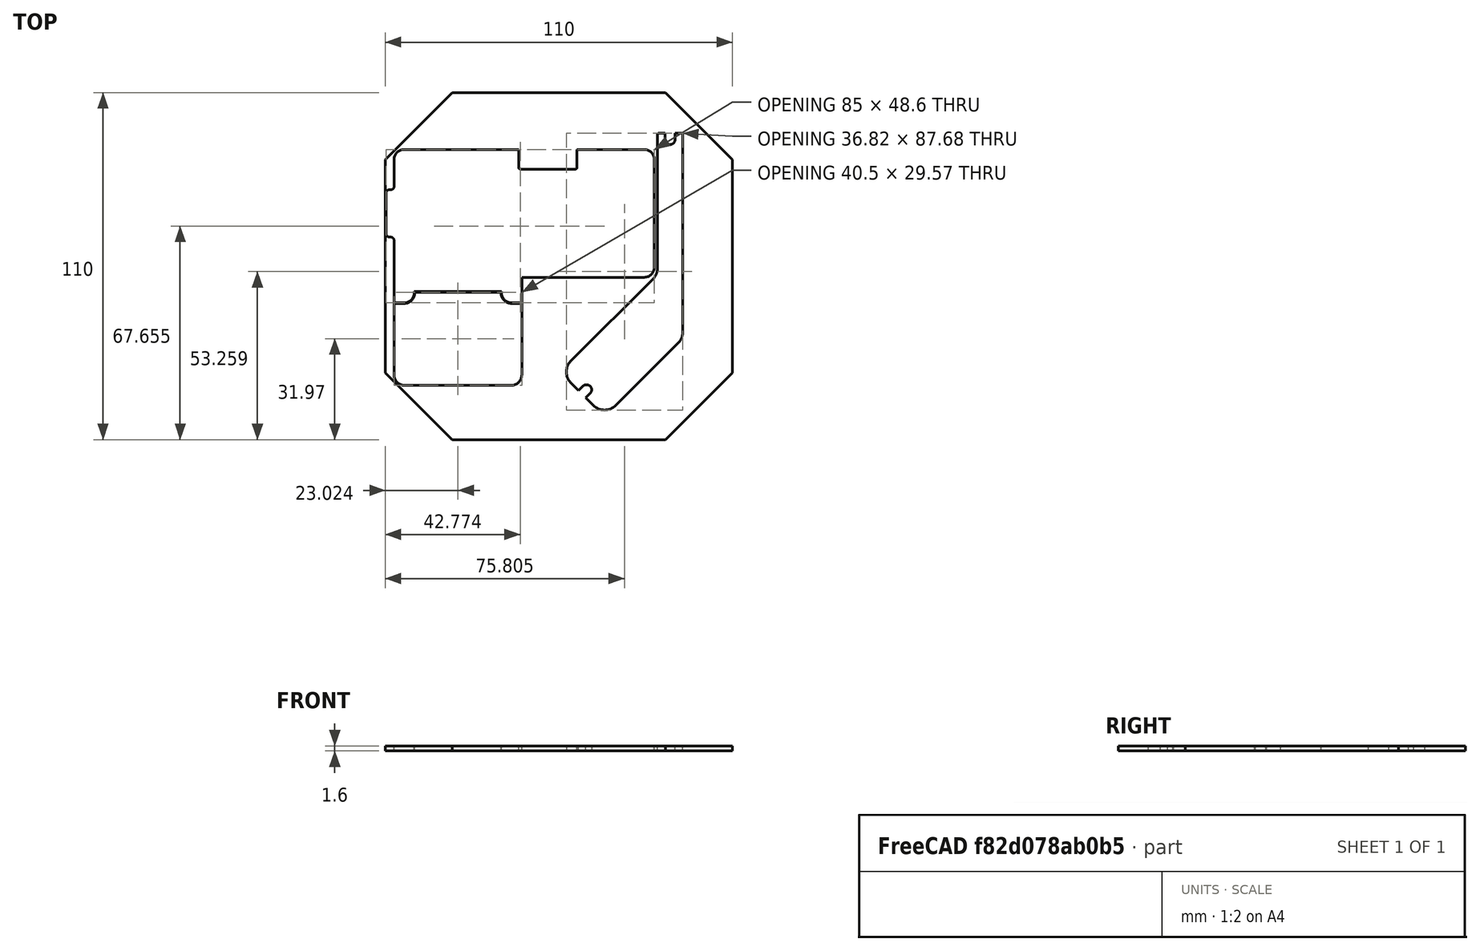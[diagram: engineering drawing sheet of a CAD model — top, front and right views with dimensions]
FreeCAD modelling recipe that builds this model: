
FCSTD DOCUMENT  (FreeCAD 1.0R39285 (Git))
Label: PCB_layout
License: All rights reserved
LicenseURL: https://en.wikipedia.org/wiki/All_rights_reserved
objects: PartDesign::Body×2, Sketcher::SketchObject×1, PartDesign::Pad×1
note: 7 computed .brp shape members not serialized (recipe doc carries the construction recipe); baked Part::Feature solids carry a one-line shape summary decoded from their .brp

FEATURE [Sketcher::SketchObject] Sketch
  ArcFitTolerance = 1e-06
  AttachmentSupport = -> [XY_Plane]
  FullyConstrained = false
  MakeInternals = false
  MapMode = 5
  sketch-geometry (149):
    g0: LineSegment StartX=43.2741 StartY=51.4547 StartZ=0 EndX=82.0741 EndY=51.4547 EndZ=0
    g1: LineSegment StartX=2.77413 StartY=88.7547 StartZ=0 EndX=2.77413 EndY=80.2047 EndZ=0
    g2: LineSegment StartX=5.97413 StartY=91.9547 StartZ=0 EndX=42.2741 EndY=91.9547 EndZ=0
    g3: LineSegment StartX=85.2741 StartY=88.7547 StartZ=0 EndX=85.2741 EndY=54.6547 EndZ=0
    g4: ArcOfCircle CenterX=82.0741 CenterY=88.7547 CenterZ=0 NormalX=0 NormalY=0 NormalZ=1 AngleXU=0 Radius=3.2 StartAngle=2e-16 EndAngle=1.5708
    g5: ArcOfCircle CenterX=5.97413 CenterY=88.7547 CenterZ=0 NormalX=0 NormalY=0 NormalZ=1 AngleXU=0 Radius=3.2 StartAngle=1.5708 EndAngle=3.14159
    g6: GeomPoint [constr] X=2.77413 Y=91.9547 Z=0
    g7: ArcOfCircle CenterX=82.0741 CenterY=54.6547 CenterZ=0 NormalX=0 NormalY=0 NormalZ=1 AngleXU=0 Radius=3.2 StartAngle=4.71239 EndAngle=6.28319
    g8: GeomPoint [constr] X=85.2741 Y=51.4547 Z=0
    g9: LineSegment StartX=1.77413 StartY=79.2047 StartZ=0 EndX=1.27413 EndY=79.2047 EndZ=0
    g10: LineSegment StartX=0.274134 StartY=78.2047 StartZ=0 EndX=0.274134 EndY=65.2047 EndZ=0
    g11: LineSegment StartX=1.27413 StartY=64.2047 StartZ=0 EndX=1.77413 EndY=64.2047 EndZ=0
    g12: ArcOfCircle CenterX=1.27413 CenterY=65.2047 CenterZ=0 NormalX=0 NormalY=0 NormalZ=1 AngleXU=0 Radius=1 StartAngle=3.14159 EndAngle=4.71239
    g13: GeomPoint [constr] X=0.274134 Y=64.2047 Z=0
    g14: ArcOfCircle CenterX=1.27413 CenterY=78.2047 CenterZ=0 NormalX=0 NormalY=0 NormalZ=1 AngleXU=0 Radius=1 StartAngle=1.5708 EndAngle=3.14159
    g15: GeomPoint [constr] X=0.274134 Y=79.2047 Z=0
    g16: LineSegment StartX=2.77413 StartY=63.2047 StartZ=0 EndX=2.77413 EndY=43.3547 EndZ=0
    g17: ArcOfCircle CenterX=1.77413 CenterY=63.2047 CenterZ=0 NormalX=0 NormalY=0 NormalZ=1 AngleXU=0 Radius=1 StartAngle=3.4e-15 EndAngle=1.5708
    g18: ArcOfCircle CenterX=1.77413 CenterY=80.2047 CenterZ=0 NormalX=0 NormalY=0 NormalZ=1 AngleXU=0 Radius=1 StartAngle=4.71239 EndAngle=6.28319
    g19: GeomPoint [constr] X=2.77413 Y=79.2047 Z=0
    g20: GeomPoint X=85.2741 Y=71.7047 Z=0
    g21: GeomPoint X=0.274134 Y=71.7047 Z=0
    g22: LineSegment StartX=6.17413 StartY=17.1847 StartZ=0 EndX=39.8741 EndY=17.1847 EndZ=0
    g23: LineSegment StartX=2.77413 StartY=43.1547 StartZ=0 EndX=2.77413 EndY=20.5847 EndZ=0
    g24: LineSegment StartX=43.2741 StartY=43.1547 StartZ=0 EndX=43.2741 EndY=20.5847 EndZ=0
    g25: ArcOfCircle CenterX=6.17413 CenterY=20.5847 CenterZ=0 NormalX=0 NormalY=0 NormalZ=1 AngleXU=0 Radius=3.4 StartAngle=3.14159 EndAngle=4.71239
    g26: GeomPoint [constr] X=2.77413 Y=17.1847 Z=0
    g27: ArcOfCircle CenterX=39.8741 CenterY=20.5847 CenterZ=0 NormalX=0 NormalY=0 NormalZ=1 AngleXU=0 Radius=3.4 StartAngle=4.71239 EndAngle=6.28319
    g28: GeomPoint [constr] X=43.2741 Y=17.1847 Z=0
    g29: LineSegment StartX=2.77413 StartY=43.3547 StartZ=0 EndX=6.00966 EndY=43.3547 EndZ=0
    g30: LineSegment StartX=9.20966 StartY=46.5547 StartZ=0 EndX=9.20966 EndY=46.9547 EndZ=0
    g31: ArcOfCircle CenterX=6.00966 CenterY=46.5547 CenterZ=0 NormalX=0 NormalY=0 NormalZ=1 AngleXU=0 Radius=3.2 StartAngle=4.71239 EndAngle=6.28319
    g32: GeomPoint [constr] X=9.20966 Y=43.3547 Z=0
    g33: LineSegment StartX=2.77413 StartY=43.1547 StartZ=0 EndX=5.94913 EndY=43.1547 EndZ=0
    g34: LineSegment StartX=9.34913 StartY=46.5547 StartZ=0 EndX=9.34913 EndY=46.7547 EndZ=0
    g35: LineSegment StartX=9.34913 StartY=46.7547 StartZ=0 EndX=36.6991 EndY=46.7547 EndZ=0
    g36: LineSegment StartX=36.6991 StartY=46.7547 StartZ=0 EndX=36.6991 EndY=46.5547 EndZ=0
    g37: LineSegment StartX=43.2741 StartY=43.1547 StartZ=0 EndX=40.0991 EndY=43.1547 EndZ=0
    g38: ArcOfCircle CenterX=5.94913 CenterY=46.5547 CenterZ=0 NormalX=0 NormalY=0 NormalZ=1 AngleXU=0 Radius=3.4 StartAngle=4.71239 EndAngle=6.28319
    g39: GeomPoint [constr] X=9.34913 Y=43.1547 Z=0
    g40: ArcOfCircle CenterX=40.0991 CenterY=46.5547 CenterZ=0 NormalX=0 NormalY=0 NormalZ=1 AngleXU=0 Radius=3.4 StartAngle=3.14159 EndAngle=4.71239
    g41: GeomPoint [constr] X=36.6991 Y=43.1547 Z=0
    g42: LineSegment StartX=42.2741 StartY=91.9547 StartZ=0 EndX=42.2741 EndY=86.2547 EndZ=0
    g43: LineSegment StartX=42.7741 StartY=85.7547 StartZ=0 EndX=60.2741 EndY=85.7547 EndZ=0
    g44: LineSegment StartX=60.7741 StartY=86.2547 StartZ=0 EndX=60.7741 EndY=91.9547 EndZ=0
    g45: GeomPoint X=51.5241 Y=85.7547 Z=0
    g46: LineSegment StartX=60.7741 StartY=91.9547 StartZ=0 EndX=82.0741 EndY=91.9547 EndZ=0
    g47: ArcOfCircle CenterX=60.2741 CenterY=86.2547 CenterZ=0 NormalX=0 NormalY=0 NormalZ=1 AngleXU=0 Radius=0.5 StartAngle=4.71239 EndAngle=6.28319
    g48: GeomPoint [constr] X=60.7741 Y=85.7547 Z=0
    g49: ArcOfCircle CenterX=42.7741 CenterY=86.2547 CenterZ=0 NormalX=0 NormalY=0 NormalZ=1 AngleXU=0 Radius=0.5 StartAngle=3.14159 EndAngle=4.71239
    g50: GeomPoint [constr] X=42.2741 Y=85.7547 Z=0
    g51: LineSegment StartX=43.2741 StartY=51.4547 StartZ=0 EndX=43.2741 EndY=43.3547 EndZ=0
    g52: LineSegment StartX=40.0386 StartY=43.3547 StartZ=0 EndX=43.2741 EndY=43.3547 EndZ=0
    g53: ArcOfCircle CenterX=40.0386 CenterY=46.5547 CenterZ=0 NormalX=0 NormalY=0 NormalZ=1 AngleXU=0 Radius=3.2 StartAngle=3.14159 EndAngle=4.71239
    g54: LineSegment StartX=0 StartY=88.7868 StartZ=0 EndX=21.2132 EndY=110 EndZ=0
    g55: LineSegment StartX=21.2132 StartY=110 StartZ=0 EndX=88.7868 EndY=110 EndZ=0
    g56: LineSegment StartX=88.7868 StartY=110 StartZ=0 EndX=110 EndY=88.7868 EndZ=0
    g57: LineSegment StartX=0 StartY=88.7868 StartZ=0 EndX=0 EndY=21.2132 EndZ=0
    g58: LineSegment StartX=110 StartY=88.7868 StartZ=0 EndX=110 EndY=21.2132 EndZ=0
    g59: LineSegment StartX=0 StartY=21.2132 StartZ=0 EndX=21.2132 EndY=0 EndZ=0
    g60: LineSegment StartX=110 StartY=21.2132 StartZ=0 EndX=88.7868 EndY=0 EndZ=0
    g61: LineSegment StartX=88.7868 StartY=0 StartZ=0 EndX=21.2132 EndY=0 EndZ=0
    g62: GeomPoint X=55 Y=110 Z=0
    g63: GeomPoint X=110 Y=55 Z=0
    g64: GeomPoint X=55 Y=0 Z=0
    g65: GeomPoint X=0 Y=55 Z=0
    g66: LineSegment [constr] StartX=55 StartY=110 StartZ=0 EndX=55 EndY=0 EndZ=0
    g67: LineSegment [constr] StartX=0 StartY=55 StartZ=0 EndX=110 EndY=55 EndZ=0
    g68: GeomPoint X=55 Y=55 Z=0
    g69: GeomPoint X=55 Y=55 Z=0
    g70: LineSegment StartX=9.20966 StartY=46.9547 StartZ=0 EndX=36.8386 EndY=46.9547 EndZ=0
    g71: LineSegment StartX=36.8386 StartY=46.5547 StartZ=0 EndX=36.8386 EndY=46.9547 EndZ=0
    g72: LineSegment StartX=144.044 StartY=96.1703 StartZ=0 EndX=147.544 EndY=96.1703 EndZ=0
    g73: LineSegment StartX=152.448 StartY=96.1703 StartZ=0 EndX=157.044 EndY=91.5741 EndZ=0
    g74: LineSegment StartX=142.044 StartY=94.1703 StartZ=0 EndX=142.044 EndY=23.1703 EndZ=0
    g75: LineSegment StartX=144.044 StartY=21.1703 StartZ=0 EndX=147.544 EndY=21.1703 EndZ=0
    g76: LineSegment StartX=152.448 StartY=21.1703 StartZ=0 EndX=157.044 EndY=25.7665 EndZ=0
    g77: LineSegment StartX=157.044 StartY=25.7665 StartZ=0 EndX=157.044 EndY=91.5741 EndZ=0
    g78: ArcOfCircle CenterX=144.044 CenterY=94.1703 CenterZ=0 NormalX=0 NormalY=0 NormalZ=1 AngleXU=0 Radius=2 StartAngle=1.5708 EndAngle=3.14159
    g79: GeomPoint [constr] X=142.044 Y=96.1703 Z=0
    g80: ArcOfCircle CenterX=144.044 CenterY=23.1703 CenterZ=0 NormalX=0 NormalY=0 NormalZ=1 AngleXU=0 Radius=2 StartAngle=3.14159 EndAngle=4.71239
    g81: GeomPoint [constr] X=142.044 Y=21.1703 Z=0
    g82: Circle [constr] CenterX=223.268 CenterY=-57.8954 CenterZ=0 NormalX=0 NormalY=0 NormalZ=1 AngleXU=0 Radius=40
    g83: LineSegment StartX=260.309 StartY=-42.7984 StartZ=0 EndX=249.349 EndY=-27.568 EndZ=0
    g84: LineSegment StartX=249.349 StartY=-27.568 StartZ=0 EndX=232.65 EndY=-19.0113 EndZ=0
    g85: LineSegment StartX=232.65 StartY=-19.0113 StartZ=0 EndX=213.886 EndY=-19.0113 EndZ=0
    g86: LineSegment StartX=213.886 StartY=-19.0113 StartZ=0 EndX=197.186 EndY=-27.568 EndZ=0
    g87: LineSegment StartX=197.186 StartY=-27.568 StartZ=0 EndX=186.226 EndY=-42.7984 EndZ=0
    g88: LineSegment StartX=186.226 StartY=-42.7984 StartZ=0 EndX=186.226 EndY=-56.2954 EndZ=0
    g89: LineSegment StartX=186.226 StartY=-72.9924 StartZ=0 EndX=197.186 EndY=-88.2229 EndZ=0
    g90: LineSegment StartX=197.186 StartY=-88.2229 StartZ=0 EndX=213.886 EndY=-96.7796 EndZ=0
    g91: LineSegment StartX=213.886 StartY=-96.7796 StartZ=0 EndX=232.65 EndY=-96.7796 EndZ=0
    g92: LineSegment StartX=232.65 StartY=-96.7796 StartZ=0 EndX=249.349 EndY=-88.2229 EndZ=0
    g93: LineSegment StartX=249.349 StartY=-88.2229 StartZ=0 EndX=260.309 EndY=-72.9924 EndZ=0
    g94: LineSegment StartX=260.309 StartY=-72.9924 StartZ=0 EndX=260.309 EndY=-59.4954 EndZ=0
    g95: Circle [constr] CenterX=223.268 CenterY=-57.8954 CenterZ=0 NormalX=0 NormalY=0 NormalZ=1 AngleXU=0 Radius=40
    g96: ArcOfCircle CenterX=149.044 CenterY=25.1703 CenterZ=0 NormalX=0 NormalY=0 NormalZ=1 AngleXU=0 Radius=1.5 StartAngle=6e-16 EndAngle=3.14159
    g97: LineSegment StartX=147.544 StartY=25.1703 StartZ=0 EndX=147.544 EndY=21.1703 EndZ=0
    g98: LineSegment StartX=150.544 StartY=25.1703 StartZ=0 EndX=150.544 EndY=21.1703 EndZ=0
    g99: ArcOfCircle CenterX=149.044 CenterY=92.1703 CenterZ=0 NormalX=0 NormalY=0 NormalZ=1 AngleXU=0 Radius=1.5 StartAngle=3.14159 EndAngle=6.28319
    g100: LineSegment StartX=147.544 StartY=92.1703 StartZ=0 EndX=147.544 EndY=96.1703 EndZ=0
    g101: LineSegment StartX=150.544 StartY=92.1703 StartZ=0 EndX=150.544 EndY=96.1703 EndZ=0
    g102: LineSegment StartX=150.544 StartY=21.1703 StartZ=0 EndX=152.448 EndY=21.1703 EndZ=0
    g103: LineSegment StartX=150.544 StartY=96.1703 StartZ=0 EndX=152.448 EndY=96.1703 EndZ=0
    g104: GeomPoint X=23.0241 Y=46.7547 Z=0
    g105: GeomPoint X=23.0241 Y=46.9547 Z=0
    g106: LineSegment StartX=86.2148 StartY=96.5982 StartZ=0 EndX=86.2148 EndY=54.0394 EndZ=0
    g107: LineSegment StartX=85.0433 StartY=51.2109 StartZ=0 EndX=58.8595 EndY=25.0272 EndZ=0
    g108: LineSegment StartX=58.8595 StartY=17.9561 StartZ=0 EndX=61.2637 EndY=15.5519 EndZ=0
    g109: LineSegment StartX=73.0016 StartY=10.885 StartZ=0 EndX=93.0433 EndY=30.9267 EndZ=0
    g110: LineSegment StartX=94.2148 StartY=33.7551 StartZ=0 EndX=94.2148 EndY=96.5982 EndZ=0
    g111: LineSegment StartX=86.7148 StartY=97.0982 StartZ=0 EndX=88.6148 EndY=97.0982 EndZ=0
    g112: GeomPoint X=62.395 Y=14.4206 Z=0
    g113: GeomPoint X=90.2148 Y=97.0982 Z=0
    g114: ArcOfCircle CenterX=63.8092 CenterY=15.8348 CenterZ=0 NormalX=0 NormalY=0 NormalZ=1 AngleXU=0 Radius=1.6 StartAngle=5.49779 EndAngle=8.63938
    g115: LineSegment [constr] StartX=62.395 StartY=14.4206 StartZ=0 EndX=71.525 EndY=23.5506 EndZ=0
    g116: LineSegment [constr] StartX=90.2148 StartY=97.0982 StartZ=0 EndX=90.2148 EndY=87.5282 EndZ=0
    g117: ArcOfCircle CenterX=90.2148 CenterY=95.0982 CenterZ=0 NormalX=0 NormalY=0 NormalZ=1 AngleXU=0 Radius=1.6 StartAngle=3.14159 EndAngle=6.28319
    g118: LineSegment StartX=88.6148 StartY=95.0982 StartZ=0 EndX=88.6148 EndY=97.0982 EndZ=0
    g119: LineSegment StartX=91.8148 StartY=95.0982 StartZ=0 EndX=91.8148 EndY=97.0982 EndZ=0
    g120: LineSegment StartX=62.6779 StartY=16.9661 StartZ=0 EndX=61.2637 EndY=15.5519 EndZ=0
    g121: LineSegment StartX=64.9406 StartY=14.7034 StartZ=0 EndX=63.5264 EndY=13.2892 EndZ=0
    g122: LineSegment [constr] StartX=110.074 StartY=76.1495 StartZ=0 EndX=94.3736 EndY=76.1495 EndZ=0
    g123: LineSegment StartX=91.8148 StartY=97.0982 StartZ=0 EndX=93.7148 EndY=97.0982 EndZ=0
    g124: LineSegment StartX=63.5264 StartY=13.2892 StartZ=0 EndX=65.9306 EndY=10.885 EndZ=0
    g125: ArcOfCircle CenterX=82.2148 CenterY=54.0394 CenterZ=0 NormalX=0 NormalY=0 NormalZ=1 AngleXU=0 Radius=4 StartAngle=5.49779 EndAngle=6.28319
    g126: GeomPoint [constr] X=86.2148 Y=52.3825 Z=0
    g127: ArcOfCircle CenterX=90.2148 CenterY=33.7551 CenterZ=0 NormalX=0 NormalY=0 NormalZ=1 AngleXU=0 Radius=4 StartAngle=5.49779 EndAngle=6.28319
    g128: GeomPoint [constr] X=94.2148 Y=32.0982 Z=0
    g129: ArcOfCircle CenterX=62.395 CenterY=21.4916 CenterZ=0 NormalX=0 NormalY=0 NormalZ=1 AngleXU=0 Radius=5 StartAngle=2.35619 EndAngle=3.92699
    g130: GeomPoint [constr] X=55.324 Y=21.4916 Z=0
    g131: ArcOfCircle CenterX=69.4661 CenterY=14.4206 CenterZ=0 NormalX=0 NormalY=0 NormalZ=1 AngleXU=0 Radius=5 StartAngle=3.92699 EndAngle=5.49779
    g132: GeomPoint [constr] X=69.4661 Y=7.34949 Z=0
    g133: ArcOfCircle CenterX=86.7148 CenterY=96.5982 CenterZ=0 NormalX=0 NormalY=0 NormalZ=1 AngleXU=0 Radius=0.5 StartAngle=1.5708 EndAngle=3.14159
    g134: GeomPoint [constr] X=86.2148 Y=97.0982 Z=0
    g135: ArcOfCircle CenterX=93.7148 CenterY=96.5982 CenterZ=0 NormalX=0 NormalY=0 NormalZ=1 AngleXU=0 Radius=0.5 StartAngle=-4.4e-15 EndAngle=1.5708
    g136: GeomPoint [constr] X=94.2148 Y=97.0982 Z=0
    g137: GeomPoint X=186.226 Y=-57.8954 Z=0
    g138: GeomPoint X=260.309 Y=-57.8954 Z=0
    g139: LineSegment [constr] StartX=186.226 StartY=-57.8954 StartZ=0 EndX=172.847 EndY=-57.8954 EndZ=0
    g140: LineSegment [constr] StartX=260.309 StartY=-57.8954 StartZ=0 EndX=273.688 EndY=-57.8954 EndZ=0
    g141: ArcOfCircle CenterX=183.226 CenterY=-57.8954 CenterZ=0 NormalX=0 NormalY=0 NormalZ=1 AngleXU=0 Radius=1.6 StartAngle=1.5708 EndAngle=4.71239
    g142: ArcOfCircle CenterX=263.309 CenterY=-57.8954 CenterZ=0 NormalX=0 NormalY=0 NormalZ=1 AngleXU=0 Radius=1.6 StartAngle=4.71239 EndAngle=7.85398
    g143: LineSegment StartX=183.226 StartY=-56.2954 StartZ=0 EndX=186.226 EndY=-56.2954 EndZ=0
    g144: LineSegment StartX=183.226 StartY=-59.4954 StartZ=0 EndX=186.226 EndY=-59.4954 EndZ=0
    g145: LineSegment StartX=263.309 StartY=-56.2954 StartZ=0 EndX=260.309 EndY=-56.2954 EndZ=0
    g146: LineSegment StartX=263.309 StartY=-59.4954 StartZ=0 EndX=260.309 EndY=-59.4954 EndZ=0
    g147: LineSegment StartX=260.309 StartY=-56.2954 StartZ=0 EndX=260.309 EndY=-42.7984 EndZ=0
    g148: LineSegment StartX=186.226 StartY=-59.4954 StartZ=0 EndX=186.226 EndY=-72.9924 EndZ=0
  constraints (349):
    c: Horizontal(g0)
    c: Vertical(g1)
    c: Perpendicular(g-2,g2)
    c: Vertical(g3)
    c: Tangent(g3,g4) = 1.5708
    c: Radius(g4) = 3.2
    c: PointOnObject(g6,g2)
    c: PointOnObject(g6,g1)
    c: Tangent(g2,g5) = 1.5708
    c: Tangent(g1,g5) = -1.5708
    c: Equal(g4,g5)
    c: PointOnObject(g8,g0)
    c: PointOnObject(g8,g3)
    c: Tangent(g0,g7) = -1.5708
    c: Tangent(g3,g7) = 1.5708
    c: Equal(g4,g7)
    c: Horizontal(g9)
    c: Horizontal(g11)
    c: Vertical(g10)
    c: Distance(g15,g19) = 2.5
    c: Distance(g3,g10) = 85
    c: PointOnObject(g13,g10)
    c: PointOnObject(g13,g11)
    c: Tangent(g10,g12) = -1.5708
    c: Tangent(g11,g12) = -1.5708
    c: PointOnObject(g15,g10)
    c: PointOnObject(g15,g9)
    c: Tangent(g10,g14) = -1.5708
    c: Tangent(g9,g14) = -1.5708
    c: Tangent(g11,g17) = 1.5708
    c: Tangent(g16,g17) = 1.5708
    c: PointOnObject(g19,g9)
    c: PointOnObject(g19,g1)
    c: Tangent(g9,g18) = 1.5708
    c: Tangent(g1,g18) = 1.5708
    c: Radius(g14) = 1
    c: Equal(g14,g18)
    c: Equal(g14,g12)
    c: Equal(g17,g12)
    c: Distance(g11,g9) = 15
    c: Vertical(g16)
    c: Symmetric(g3,g3,g20)
    c: Symmetric(g10,g10,g21)
    c: Horizontal(g21,g20)
    c: Horizontal(g22)
    c: Vertical(g23)
    c: Vertical(g24)
    c: PointOnObject(g26,g22)
    c: PointOnObject(g26,g23)
    c: Tangent(g22,g25) = -1.5708
    c: Tangent(g23,g25) = -1.5708
    c: PointOnObject(g28,g22)
    c: PointOnObject(g28,g24)
    c: Tangent(g22,g27) = -1.5708
    c: Tangent(g24,g27) = 1.5708
    c: Distance(g24,g23) = 40.5
    c: Coincident(g29,g16)
    c: Horizontal(g29)
    c: Vertical(g30)
    c: PointOnObject(g32,g29)
    c: PointOnObject(g32,g30)
    c: Tangent(g29,g31) = -1.5708
    c: Tangent(g30,g31) = -1.5708
    c: Radius(g31) = 3.2
    c: Coincident(g33,g23)
    c: Horizontal(g33)
    c: Vertical(g34)
    c: Coincident(g35,g34)
    c: Horizontal(g35)
    c: Coincident(g36,g35)
    c: Vertical(g36)
    c: Coincident(g37,g24)
    c: Horizontal(g37)
    c: PointOnObject(g39,g33)
    c: PointOnObject(g39,g34)
    c: Tangent(g33,g38) = -1.5708
    c: Tangent(g34,g38) = -1.5708
    c: PointOnObject(g41,g36)
    c: PointOnObject(g41,g37)
    c: Tangent(g36,g40) = -1.5708
    c: Tangent(g37,g40) = 1.5708
    c: Radius(g40) = 3.4
    c: Equal(g38,g25)
    c: Equal(g38,g27)
    c: Vertical(g42)
    c: Horizontal(g43)
    c: PointOnObject(g44,g46)
    c: Vertical(g44)
    c: Symmetric(g50,g48,g45)
    c: DistanceY(g48,g44) = 6.2
    c: DistanceX(g50,g48) = 18.5
    c: Coincident(g2,g42)
    c: PointOnObject(g46,g44)
    c: Horizontal(g46)
    c: Tangent(g46,g4) = 1.5708
    c: PointOnObject(g48,g44)
    c: PointOnObject(g48,g43)
    c: Tangent(g44,g47) = -1.5708
    c: Tangent(g43,g47) = -1.5708
    c: PointOnObject(g50,g43)
    c: PointOnObject(g50,g42)
    c: Tangent(g43,g49) = -1.5708
    c: Tangent(g42,g49) = -1.5708
    c: Radius(g49) = 0.5
    c: Equal(g44,g42)
    c: Equal(g47,g49)
    c: Vertical(g51)
    c: Horizontal(g52)
    c: Coincident(g52,g51)
    c: Tangent(g52,g53) = -1.5708
    c: Equal(g31,g53)
    c: Equal(g29,g52)
    c: Equal(g9,g11)
    c: Coincident(g55,g54)
    c: Horizontal(g55)
    c: Coincident(g56,g55)
    c: Coincident(g57,g54)
    c: Vertical(g57)
    c: Coincident(g58,g56)
    c: Vertical(g58)
    c: Coincident(g59,g57)
    c: Coincident(g60,g58)
    c: Coincident(g61,g60)
    c: Horizontal(g61)
    c: Coincident(g59,g61)
    c: Angle(g55,g56) = 2.35619
    c: Angle(g54,g55) = 2.35619
    c: Angle(g61,g59) = 2.35619
    c: Angle(g60,g61) = 2.35619
    c: Distance(g61,g55) = 110
    c: Distance(g58,g57) = 110
    c: Distance(g54,g54) = 30
    c: Equal(g54,g56)
    c: Equal(g56,g59)
    c: Equal(g60,g59)
    c: Symmetric(g55,g55,g62)
    c: Symmetric(g58,g58,g63)
    c: Symmetric(g61,g61,g64)
    c: Symmetric(g57,g57,g65)
    c: Coincident(g66,g62)
    c: Coincident(g66,g64)
    c: Coincident(g67,g65)
    c: Coincident(g67,g63)
    c: Symmetric(g66,g66,g69)
    c: Coincident(g68,g69)
    c: Vertical(g-1,g57)
    c: Horizontal(g-1,g59)
    c: Distance(g46,g0) = 40.5
    c: Distance(g1,g42) = 39.5
    c: Coincident(g0,g51)
    c: Coincident(g70,g30)
    c: Horizontal(g70)
    c: Vertical(g71)
    c: Coincident(g70,g71)
    c: Equal(g30,g71)
    c: Tangent(g71,g53) = 1.5708
    c: Distance(g29,g70) = 3.6
    c: Distance(g0,g70) = 4.5
    c: Distance(g22,g35) = 29.57
    c: Equal(g36,g34)
    c: DistanceY(g36,g36) = 0.2
    c: Horizontal(g72)
    c: Coincident(g73,g103)
    c: Vertical(g74)
    c: Horizontal(g75)
    c: Coincident(g76,g102)
    c: Coincident(g77,g76)
    c: Vertical(g77)
    c: Coincident(g77,g73)
    c: Angle(g72,g73) = 2.35619
    c: Angle(g76,g75) = 2.35619
    c: DistanceY(g81,g79) = 75
    c: Distance(g79,g77) = 15
    c: Distance(g76,g76) = 6.5
    c: Distance(g73,g73) = 6.5
    c: PointOnObject(g79,g72)
    c: PointOnObject(g79,g74)
    c: Tangent(g72,g78) = 1.5708
    c: Tangent(g74,g78) = -1.5708
    c: PointOnObject(g81,g74)
    c: PointOnObject(g81,g75)
    c: Tangent(g74,g80) = -1.5708
    c: Tangent(g75,g80) = -1.5708
    c: Radius(g80) = 2
    c: Equal(g80,g78)
    c: Diameter(g82) = 80
    c: Coincident(g83,g84)
    c: Coincident(g84,g85)
    c: Coincident(g85,g86)
    c: Coincident(g86,g87)
    c: Coincident(g87,g88)
    c: Coincident(g148,g89)
    c: Coincident(g89,g90)
    c: Coincident(g90,g91)
    c: Coincident(g91,g92)
    c: Coincident(g92,g93)
    c: Coincident(g93,g94)
    c: Coincident(g147,g83)
    c: Equal(g83, g84-g87) x4
    c: Equal(g83, g89-g93) x5
    c: PointOnObject(g83,g95)
    c: PointOnObject(g84,g95)
    c: PointOnObject(g85,g95)
    c: PointOnObject(g86,g95)
    c: PointOnObject(g87,g95)
    c: PointOnObject(g148,g95)
    c: PointOnObject(g89,g95)
    c: PointOnObject(g90,g95)
    c: PointOnObject(g91,g95)
    c: PointOnObject(g92,g95)
    c: PointOnObject(g93,g95)
    c: PointOnObject(g147,g95)
    c: Coincident(g95,g82)
    c: PointOnObject(g147,g82)
    c: Parallel(g85,g-1)
    c: Vertical(g97)
    c: PointOnObject(g98,g102)
    c: Vertical(g98)
    c: Vertical(g100)
    c: PointOnObject(g101,g103)
    c: Vertical(g101)
    c: Diameter(g99) = 3
    c: Diameter(g96) = 3
    c: Distance(g99,g72) = 4
    c: Distance(g96,g75) = 4
    c: Distance(g96,g74) = 7
    c: Distance(g99,g74) = 7
    c: Tangent(g96,g97) = -1.5708
    c: Tangent(g96,g98) = 1.5708
    c: Coincident(g75,g97)
    c: PointOnObject(g102,g98)
    c: Coincident(g72,g100)
    c: PointOnObject(g103,g101)
    c: Tangent(g99,g101) = -1.5708
    c: Tangent(g99,g100) = 1.5708
    c: Equal(g100,g101)
    c: Equal(g102,g103)
    c: Angle(g103,g73) = 2.35619
    c: Equal(g98,g97)
    c: Equal(g40,g38)
    c: Equal(g37,g33)
    c: Distance(g51,g16) = 40.5
    c: Symmetric(g35,g35,g104)
    c: Symmetric(g70,g70,g105)
    c: Vertical(g104,g105)
    c: Distance(g105,g104) = 0.2
    c: DistanceX(g35,g35) = 27.35
    c: Vertical(g106)
    c: Vertical(g110)
    c: Horizontal(g111)
    c: Distance(g130,g132) = 20
    c: Perpendicular(g108,g109)
    c: Perpendicular(g107,g108)
    c: DistanceX(g134,g136) = 8
    c: DistanceY(g128,g136) = 65
    c: Distance(g132,g128) = 35
    c: Symmetric(g130,g132,g112)
    c: Symmetric(g134,g136,g113)
    c: Coincident(g115,g112)
    c: PointOnObject(g114,g115)
    c: Coincident(g116,g113)
    c: Vertical(g116)
    c: PointOnObject(g117,g116)
    c: Diameter(g114) = 3.2
    c: Equal(g114,g117)
    c: Distance(g114,g108) = 2
    c: DistanceY(g117,g113) = 2
    c: Vertical(g118)
    c: Vertical(g119)
    c: Perpendicular(g108,g121)
    c: Distance(g122) = 15.7
    c: Horizontal(g122)
    c: Tangent(g117,g118) = 1.5708
    c: Tangent(g117,g119) = -1.5708
    c: Coincident(g111,g118)
    c: Coincident(g123,g119)
    c: Tangent(g114,g120) = -1.5708
    c: Perpendicular(g108,g120) = 4.71239
    c: Tangent(g114,g121) = 1.5708
    c: Equal(g120,g121)
    c: Equal(g118,g119)
    c: Coincident(g124,g121)
    c: Perpendicular(g109,g124)
    c: Perpendicular(g108,g115)
    c: PointOnObject(g126,g107)
    c: PointOnObject(g126,g106)
    c: Tangent(g107,g125) = 1.5708
    c: Tangent(g106,g125) = 1.5708
    c: PointOnObject(g128,g109)
    c: PointOnObject(g128,g110)
    c: Tangent(g109,g127) = -1.5708
    c: Tangent(g110,g127) = -1.5708
    c: PointOnObject(g130,g108)
    c: PointOnObject(g130,g107)
    c: Tangent(g108,g129) = -1.5708
    c: Tangent(g107,g129) = -1.5708
    c: PointOnObject(g132,g109)
    c: PointOnObject(g132,g124)
    c: Tangent(g109,g131) = -1.5708
    c: Tangent(g124,g131) = -1.5708
    c: PointOnObject(g134,g111)
    c: PointOnObject(g134,g106)
    c: Tangent(g111,g133) = 1.5708
    c: Tangent(g106,g133) = -1.5708
    c: PointOnObject(g136,g123)
    c: PointOnObject(g136,g110)
    c: Tangent(g123,g135) = 1.5708
    c: Tangent(g110,g135) = -1.5708
    c: Radius(g135) = 0.5
    c: Equal(g135,g133)
    c: Radius(g125) = 4
    c: Equal(g125,g127)
    c: Horizontal(g123)
    c: Radius(g131) = 5
    c: Equal(g131,g129)
    c: DistanceX(g115,g115) = 9.13
    c: DistanceY(g116,g116) = 9.57
    c: Angle(g106,g107) = 2.35619
    c: Symmetric(g88,g148,g137)
    c: Symmetric(g94,g147,g138)
    c: Coincident(g139,g137)
    c: Horizontal(g139)
    c: Coincident(g140,g138)
    c: Horizontal(g140)
    c: PointOnObject(g141,g139)
    c: PointOnObject(g142,g140)
    c: Equal(g141,g142)
    c: Diameter(g141) = 3.2
    c: Distance(g142,g94) = 3
    c: Distance(g141,g88) = 3
    c: Equal(g139,g140)
    c: Horizontal(g143)
    c: PointOnObject(g144,g148)
    c: Horizontal(g144)
    c: Horizontal(g145)
    c: Horizontal(g146)
    c: Coincident(g94,g146)
    c: Coincident(g147,g145)
    c: Tangent(g142,g146) = 1.5708
    c: Tangent(g142,g145) = -1.5708
    c: Tangent(g141,g143) = 1.5708
    c: Tangent(g141,g144) = -1.5708
    c: PointOnObject(g148,g144)
    c: Coincident(g88,g143)
    c: Equal(g143,g144)
    c: Equal(g145,g146)
    c: Equal(g145,g143)
    c: Equal(g148,g94)
    c: Vertical(g88)
FEATURE [PartDesign::Pad] Pad
  Direction = (0,0,1)
  Length = 1.6
  Length2 = 10
  Profile = -> Sketch
  ReferenceAxis = -> Sketch [N_Axis]
  Refine = true
  Suppressed = false
  Type = 0
FEATURE [PartDesign::Body] Body
  AllowCompound = false
  Group = -> [Sketch,Pad]
  Origin = -> Origin
  Tip = -> Pad
FEATURE [PartDesign::Body] Body001
  AllowCompound = false
  Origin = -> Origin001
